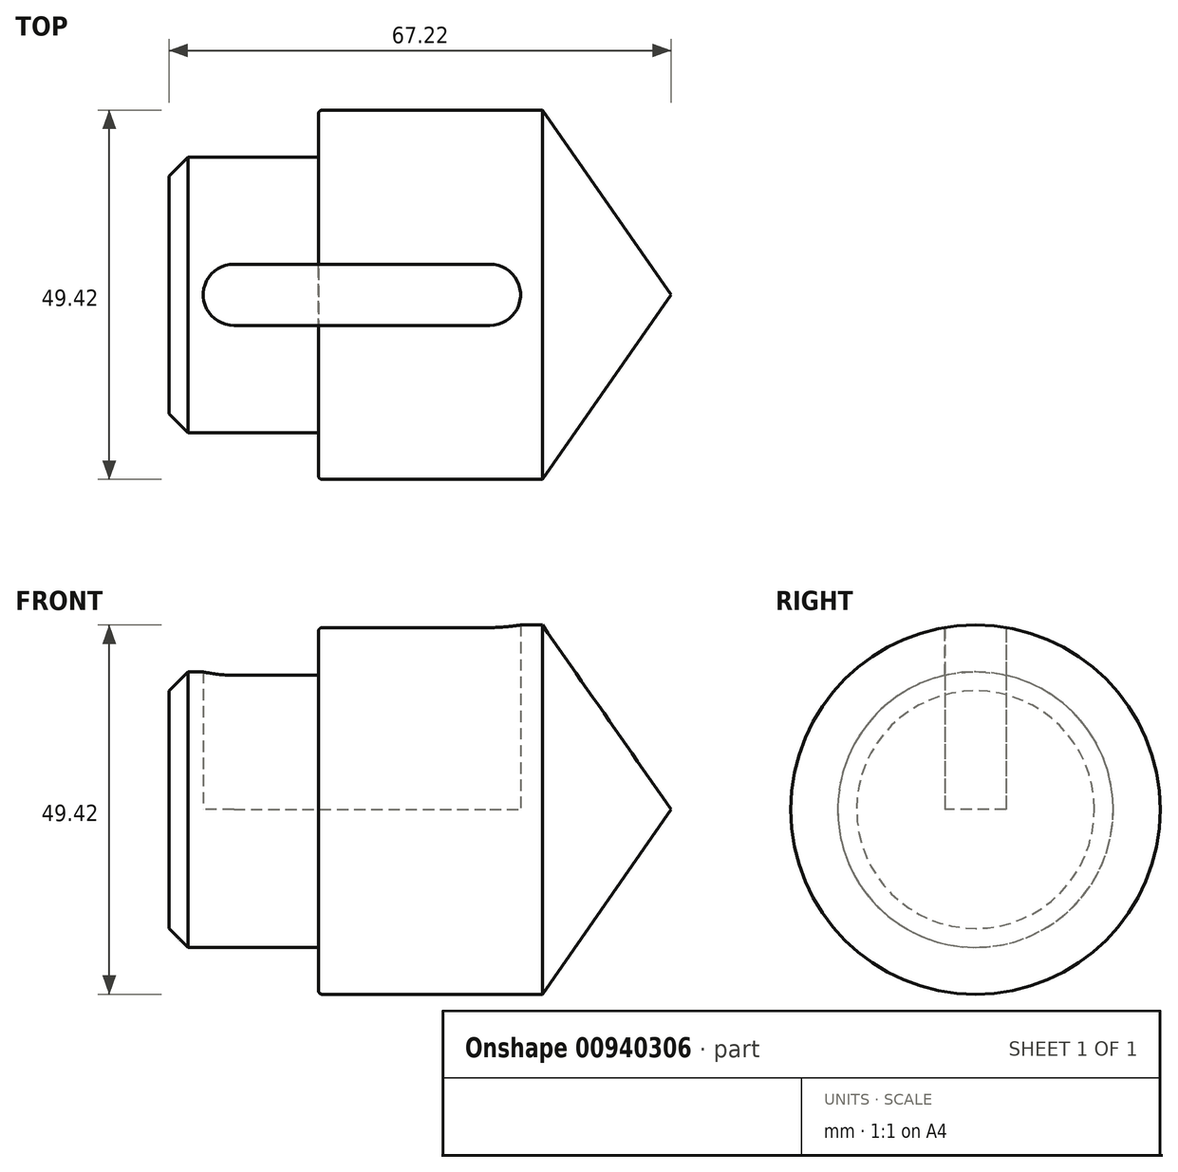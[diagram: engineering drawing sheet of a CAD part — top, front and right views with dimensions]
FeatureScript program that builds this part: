
annotation { "Feature Type Name" : "Feature", "Feature Type Description" : "" }
export const myFeature = defineFeature(function(context is Context, id is Id, definition is map)
    precondition{}
    {
        {
            var Q0;
            Q0=qCreatedBy(makeId("Front.planeOp"),FACE);
            var sketch = newSketch(context, id + "F0", { "sketchPlane" : qUnion([Q0])});
            skLineSegment(sketch, "E0", {"start": v(67.22, 0) * mm, "end": v(0, 0) * mm, "construction": true});
            skLineSegment(sketch, "E1", {"start": v(0, 0) * mm, "end": v(0, 18.44) * mm});
            skLineSegment(sketch, "E2", {"start": v(20, 18.44) * mm, "end": v(0, 18.44) * mm});
            skLineSegment(sketch, "E3", {"start": v(20, 24.71) * mm, "end": v(20, 18.44) * mm});
            skLineSegment(sketch, "E4", {"start": v(49.96, 24.71) * mm, "end": v(20, 24.71) * mm});
            skLineSegment(sketch, "E5", {"start": v(67.22, 0) * mm, "end": v(49.96, 24.71) * mm});
            skLineSegment(sketch, "E6", {"start": v(67.22, 0) * mm, "end": v(0, 0) * mm});
            skSolve(sketch);
        }
        {
            var Q0;
            Q0=makeQuery(id+"F0.imprint","IMPRINT",FACE,{"disambiguationData":[TD([[makeQuery(id+"F0.imprint","IMPRINT",EDGE,{"derivedFrom":sQuery(id+"F0.wireOp",EDGE,"E1")}),-1.0]])]});
            var Q1;
            Q1=sQuery(id+"F0.wireOp",EDGE,"E0");
            revolve(context, id + "F1", {"surfaceOperationType" : NewSurfaceOperationType.NEW, "entities" : qUnion([Q0]), "axis" : qUnion([Q1]), "revolveType" : RevolveType.FULL});
        }
        {
            var Q0;
            Q0=qCreatedBy(makeId("Top.planeOp"),FACE);
            var sketch = newSketch(context, id + "F2", { "sketchPlane" : qUnion([Q0])});
            skLineSegment(sketch, "E7", {"start": v(8.68, 4.1) * mm, "end": v(42.95, 4.1) * mm});
            skArc(sketch, "E8", {"start": v(42.95, 4.1) * mm, "mid": v(47.05, 0) * mm, "end": v(42.95, -4.1) * mm});
            skArc(sketch, "E9", {"start": v(8.68, 4.1) * mm, "mid": v(4.58, 0) * mm, "end": v(8.68, -4.1) * mm});
            skLineSegment(sketch, "E10", {"start": v(42.95, -4.1) * mm, "end": v(8.68, -4.1) * mm});
            skSolve(sketch);
        }
        {
            var Q0;
            Q0 = qSketchRegion(id + "F2", true);
            extrude(context, id + "F3", {"entities" : qUnion([Q0]), "operationType" : NewBodyOperationType.REMOVE, "depth" : 25.4 * mm, "offsetDistance" : 25.4 * mm});
        }
        {
            var Q0;
            Q0=makeQuery(id+"F1.opRevolve","SWEPT_EDGE",EDGE,{"disambiguationData":[OSD([sQuery(id+"F0.wireOp",EDGE,"E1"),sQuery(id+"F0.wireOp",EDGE,"E2")])]});
            chamfer(context, id + "F4", {"entities" : qUnion([Q0]), "width" : 2.54 * mm, "tangentPropagation" : true});
        }
        {
            var Q0;
            Q0=makeQuery(id+"F1.opRevolve","SWEPT_EDGE",EDGE,{"disambiguationData":[OSD([sQuery(id+"F0.wireOp",EDGE,"E3"),sQuery(id+"F0.wireOp",EDGE,"E4")])]});
            fillet(context, id + "F5", {"entities" : qUnion([Q0]), "radius" : 0.5 * mm, "tangentPropagation" : true, "allowEdgeOverflow" : false});
        }
    });
